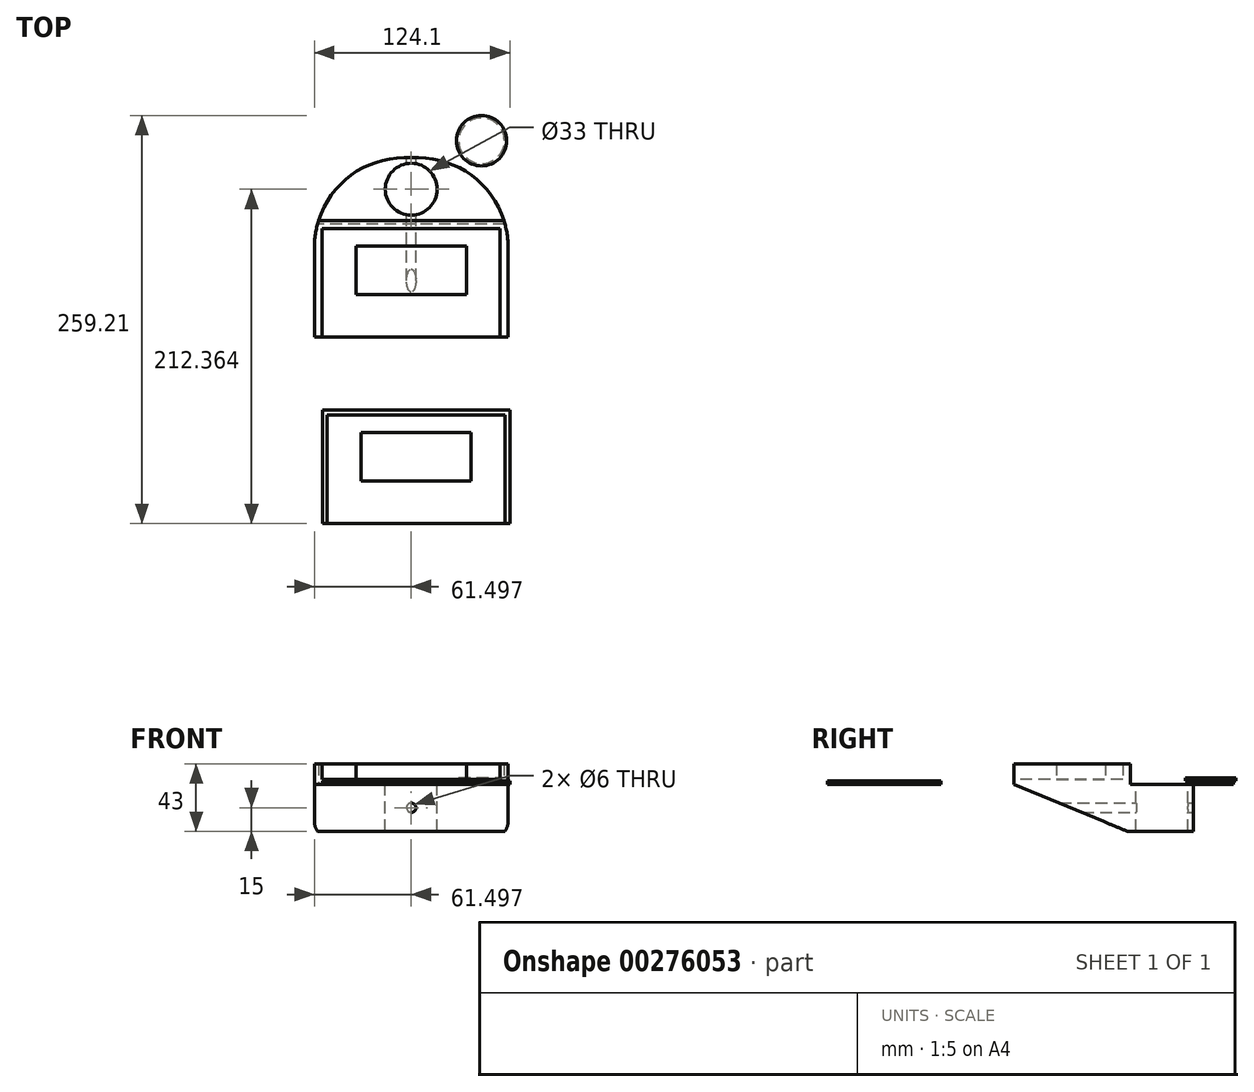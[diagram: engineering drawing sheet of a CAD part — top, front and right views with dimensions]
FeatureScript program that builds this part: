
annotation { "Feature Type Name" : "Feature", "Feature Type Description" : "" }
export const myFeature = defineFeature(function(context is Context, id is Id, definition is map)
    precondition{}
    {
        {
            var Q0;
            Q0=qCreatedBy(makeId("Top.planeOp"),FACE);
            var sketch = newSketch(context, id + "F0", { "sketchPlane" : qUnion([Q0])});
            skCircle(sketch, "E0", {"center": v(-51.44, 51.07) * mm, "radius": 14.5 * mm});
            skSolve(sketch);
        }
        {
            var Q0;
            Q0 = qSketchRegion(id + "F0", true);
            extrude(context, id + "F1", {"entities" : qUnion([Q0]), "depth" : 35 * mm});
        }
        {
            var Q0;
            Q0=makeQuery(id+"F1.opExtrude","CAP_FACE",FACE,{"disambiguationData":[OSD([sQuery(id+"F0.wireOp",EDGE,"E0")])],"isStart":false});
            var sketch = newSketch(context, id + "F2", { "sketchPlane" : qUnion([Q0])});
            skCircle(sketch, "E1", {"center": v(-51.44, 51.07) * mm, "radius": 16 * mm});
            skSolve(sketch);
        }
        {
            var Q0;
            Q0 = qSketchRegion(id + "F2", true);
            extrude(context, id + "F3", {"entities" : qUnion([Q0]), "operationType" : NewBodyOperationType.ADD, "depth" : 3 * mm});
        }
        {
            var Q0;
            Q0=makeQuery(id+"F3.opExtrude","CAP_FACE",FACE,{"disambiguationData":[OSD([sQuery(id+"F2.wireOp",EDGE,"E1")])],"isStart":false});
            var sketch = newSketch(context, id + "F4", { "sketchPlane" : qUnion([Q0])});
            skCircle(sketch, "E2", {"center": v(-51.44, 51.07) * mm, "radius": 14.5 * mm});
            skSolve(sketch);
        }
        {
            var Q0;
            Q0 = qSketchRegion(id + "F4", true);
            extrude(context, id + "F5", {"entities" : qUnion([Q0]), "operationType" : NewBodyOperationType.ADD, "depth" : 35 * mm});
        }
        {
            var Q0;
            Q0=qCreatedBy(makeId("Top.planeOp"),FACE);
            var sketch = newSketch(context, id + "F6", { "sketchPlane" : qUnion([Q0])});
            skLineSegment(sketch, "E3.bottom", {"start": v(-44.58, 8.17) * mm, "end": v(68.42, 8.17) * mm});
            skLineSegment(sketch, "E3.top", {"start": v(-44.58, -60.83) * mm, "end": v(68.42, -60.83) * mm});
            skLineSegment(sketch, "E3.left", {"start": v(-44.58, 8.17) * mm, "end": v(-44.58, -60.83) * mm});
            skLineSegment(sketch, "E3.right", {"start": v(68.42, 8.17) * mm, "end": v(68.42, -60.83) * mm});
            skSolve(sketch);
        }
        {
            var Q0;
            Q0 = qSketchRegion(id + "F6", true);
            extrude(context, id + "F7", {"entities" : qUnion([Q0]), "depth" : 3 * mm});
        }
        {
            var Q0;
            Q0=makeQuery(id+"F7.opExtrude","CAP_FACE",FACE,{"disambiguationData":[OSD([sQuery(id+"F6.wireOp",EDGE,"E3.bottom"),sQuery(id+"F6.wireOp",EDGE,"E3.top"),sQuery(id+"F6.wireOp",EDGE,"E3.left"),sQuery(id+"F6.wireOp",EDGE,"E3.right")])],"isStart":false});
            var sketch = newSketch(context, id + "F8", { "sketchPlane" : qUnion([Q0])});
            skLineSegment(sketch, "E4.bottom", {"start": v(46.92, -33.83) * mm, "end": v(-23.08, -33.83) * mm});
            skLineSegment(sketch, "E4.top", {"start": v(46.92, -2.83) * mm, "end": v(-23.08, -2.83) * mm});
            skLineSegment(sketch, "E4.left", {"start": v(46.92, -33.83) * mm, "end": v(46.92, -2.83) * mm});
            skLineSegment(sketch, "E4.right", {"start": v(-23.08, -33.83) * mm, "end": v(-23.08, -2.83) * mm});
            skPoint(sketch, "E4.middle", {"position": v(11.92, -18.33) * mm});
            skPoint(sketch, "E4.middle.positionSnap0", {"position": v(11.92, 8.17) * mm});
            skPoint(sketch, "E4.centerSnap0", {"position": v(11.92, 8.17) * mm});
            skSolve(sketch);
        }
        {
            var Q0;
            Q0 = qSketchRegion(id + "F8", true);
            extrude(context, id + "F9", {"entities" : qUnion([Q0]), "operationType" : NewBodyOperationType.ADD, "depth" : 10 * mm});
        }
        {
            var Q0;
            Q0=makeQuery(id+"F7.opExtrude","SWEPT_FACE",FACE,{"disambiguationData":[OSD([sQuery(id+"F6.wireOp",EDGE,"E3.right")])]});
            var sketch = newSketch(context, id + "F10", { "sketchPlane" : qUnion([Q0])});
            skLineSegment(sketch, "E5.bottom", {"start": v(-60.83, 0) * mm, "end": v(8.17, 0) * mm});
            skLineSegment(sketch, "E5.top", {"start": v(-60.83, 13) * mm, "end": v(8.17, 13) * mm});
            skLineSegment(sketch, "E5.left", {"start": v(-60.83, 0) * mm, "end": v(-60.83, 13) * mm});
            skLineSegment(sketch, "E5.right", {"start": v(8.17, 0) * mm, "end": v(8.17, 13) * mm});
            skSolve(sketch);
        }
        {
            var Q0;
            Q0 = qSketchRegion(id + "F10", true);
            extrude(context, id + "F11", {"entities" : qUnion([Q0]), "operationType" : NewBodyOperationType.ADD, "depth" : 5 * mm});
        }
        {
            var Q0;
            Q0=makeQuery(id+"F11.boolean.opBoolean","MERGE",FACE,{"derivedFrom":[makeQuery(id+"F7.opExtrude","SWEPT_FACE",FACE,{"disambiguationData":[OSD([sQuery(id+"F6.wireOp",EDGE,"E3.bottom")])]}),makeQuery(id+"F11.opExtrude","SWEPT_FACE",FACE,{"disambiguationData":[OSD([sQuery(id+"F10.wireOp",EDGE,"E5.right")])]})]});
            var sketch = newSketch(context, id + "F12", { "sketchPlane" : qUnion([Q0])});
            skLineSegment(sketch, "E6.bottom", {"start": v(-73.42, 13) * mm, "end": v(44.58, 13) * mm});
            skLineSegment(sketch, "E6.top", {"start": v(-73.42, 0) * mm, "end": v(44.58, 0) * mm});
            skLineSegment(sketch, "E6.left", {"start": v(-73.42, 13) * mm, "end": v(-73.42, 0) * mm});
            skLineSegment(sketch, "E6.right", {"start": v(44.58, 13) * mm, "end": v(44.58, 0) * mm});
            skSolve(sketch);
        }
        {
            var Q0;
            Q0 = qSketchRegion(id + "F12", true);
            extrude(context, id + "F13", {"entities" : qUnion([Q0]), "operationType" : NewBodyOperationType.ADD, "depth" : 5 * mm});
        }
        {
            var Q0;
            Q0=makeQuery(id+"F13.boolean.opBoolean","MERGE",FACE,{"derivedFrom":[makeQuery(id+"F7.opExtrude","SWEPT_FACE",FACE,{"disambiguationData":[OSD([sQuery(id+"F6.wireOp",EDGE,"E3.left")])]}),makeQuery(id+"F13.opExtrude","SWEPT_FACE",FACE,{"disambiguationData":[OSD([sQuery(id+"F12.wireOp",EDGE,"E6.right")])]})]});
            var sketch = newSketch(context, id + "F14", { "sketchPlane" : qUnion([Q0])});
            skLineSegment(sketch, "E7.bottom", {"start": v(-13.17, 13) * mm, "end": v(60.83, 13) * mm});
            skLineSegment(sketch, "E7.top", {"start": v(-13.17, 0) * mm, "end": v(60.83, 0) * mm});
            skLineSegment(sketch, "E7.left", {"start": v(-13.17, 13) * mm, "end": v(-13.17, 0) * mm});
            skLineSegment(sketch, "E7.right", {"start": v(60.83, 13) * mm, "end": v(60.83, 0) * mm});
            skSolve(sketch);
        }
        {
            var Q0;
            Q0 = qSketchRegion(id + "F14", true);
            extrude(context, id + "F15", {"entities" : qUnion([Q0]), "operationType" : NewBodyOperationType.ADD, "depth" : 5 * mm});
        }
        {
            var Q0;
            Q0=makeQuery(id+"F15.boolean.opBoolean","MERGE",FACE,{"derivedFrom":[makeQuery(id+"F13.boolean.opBoolean","MERGE",FACE,{"derivedFrom":[makeQuery(id+"F11.boolean.opBoolean","MERGE",FACE,{"derivedFrom":[makeQuery(id+"F7.opExtrude","CAP_FACE",FACE,{"disambiguationData":[OSD([sQuery(id+"F6.wireOp",EDGE,"E3.bottom"),sQuery(id+"F6.wireOp",EDGE,"E3.top"),sQuery(id+"F6.wireOp",EDGE,"E3.left"),sQuery(id+"F6.wireOp",EDGE,"E3.right")])],"isStart":true}),makeQuery(id+"F11.opExtrude","SWEPT_FACE",FACE,{"disambiguationData":[OSD([sQuery(id+"F10.wireOp",EDGE,"E5.bottom")])]})]}),makeQuery(id+"F13.opExtrude","SWEPT_FACE",FACE,{"disambiguationData":[OSD([sQuery(id+"F12.wireOp",EDGE,"E6.top")])]})]}),makeQuery(id+"F15.opExtrude","SWEPT_FACE",FACE,{"disambiguationData":[OSD([sQuery(id+"F14.wireOp",EDGE,"E7.top")])]})]});
            var sketch = newSketch(context, id + "F16", { "sketchPlane" : qUnion([Q0])});
            skLineSegment(sketch, "E8.bottom", {"start": v(73.42, -13.17) * mm, "end": v(-49.58, -13.17) * mm});
            skLineSegment(sketch, "E8.top", {"start": v(73.42, 60.83) * mm, "end": v(-49.58, 60.83) * mm});
            skLineSegment(sketch, "E8.left", {"start": v(73.42, -13.17) * mm, "end": v(73.42, 60.83) * mm});
            skLineSegment(sketch, "E8.right", {"start": v(-49.58, -13.17) * mm, "end": v(-49.58, 60.83) * mm});
            skSolve(sketch);
        }
        {
            var Q0;
            Q0 = qSketchRegion(id + "F16", true);
            extrude(context, id + "F17", {"entities" : qUnion([Q0]), "operationType" : NewBodyOperationType.ADD, "depth" : 30 * mm});
        }
        {
            var Q0;
            Q0=makeQuery(id+"F17.boolean.opBoolean","MERGE",FACE,{"derivedFrom":[makeQuery(id+"F15.boolean.opBoolean","MERGE",FACE,{"derivedFrom":[makeQuery(id+"F13.opExtrude","CAP_FACE",FACE,{"disambiguationData":[OSD([sQuery(id+"F12.wireOp",EDGE,"E6.bottom"),sQuery(id+"F12.wireOp",EDGE,"E6.top"),sQuery(id+"F12.wireOp",EDGE,"E6.left"),sQuery(id+"F12.wireOp",EDGE,"E6.right")])],"isStart":false}),makeQuery(id+"F15.opExtrude","SWEPT_FACE",FACE,{"disambiguationData":[OSD([sQuery(id+"F14.wireOp",EDGE,"E7.left")])]})]}),makeQuery(id+"F17.opExtrude","SWEPT_FACE",FACE,{"disambiguationData":[OSD([sQuery(id+"F16.wireOp",EDGE,"E8.bottom")])]})]});
            var sketch = newSketch(context, id + "F18", { "sketchPlane" : qUnion([Q0])});
            skPoint(sketch, "E9", {"position": v(-11.92, 0) * mm});
            skPoint(sketch, "E9.positionSnap0", {"position": v(-11.92, -30) * mm});
            skLineSegment(sketch, "E10.bottom", {"start": v(-73.42, 0) * mm, "end": v(49.58, 0) * mm});
            skLineSegment(sketch, "E10.top", {"start": v(-73.42, -30) * mm, "end": v(49.58, -30) * mm});
            skLineSegment(sketch, "E10.left", {"start": v(-73.42, 0) * mm, "end": v(-73.42, -30) * mm});
            skLineSegment(sketch, "E10.right", {"start": v(49.58, 0) * mm, "end": v(49.58, -30) * mm});
            skSolve(sketch);
        }
        {
            var Q0;
            Q0 = qSketchRegion(id + "F18", true);
            extrude(context, id + "F19", {"entities" : qUnion([Q0]), "operationType" : NewBodyOperationType.ADD, "depth" : 40 * mm});
        }
        {
            var Q0;
            Q0=makeQuery(id+"F19.opExtrude","SWEPT_FACE",FACE,{"disambiguationData":[OSD([sQuery(id+"F18.wireOp",EDGE,"E10.bottom")])]});
            var sketch = newSketch(context, id + "F20", { "sketchPlane" : qUnion([Q0])});
            skCircle(sketch, "E11", {"center": v(11.92, 33.17) * mm, "radius": 16.5 * mm});
            skPoint(sketch, "E11.centerSnap0", {"position": v(73.42, 33.17) * mm});
            skPoint(sketch, "E11.centerSnap1", {"position": v(11.92, 53.17) * mm});
            skSolve(sketch);
        }
        {
            var Q0;
            Q0 = qSketchRegion(id + "F20", true);
            extrude(context, id + "F21", {"entities" : qUnion([Q0]), "operationType" : NewBodyOperationType.REMOVE, "endBound" : BoundingType.THROUGH_ALL, "oppositeDirection" : true, "depth" : 25 * mm});
        }
        {
            var Q0;
            Q0=makeQuery(id+"F17.opExtrude","CAP_EDGE",EDGE,{"disambiguationData":[OSD([sQuery(id+"F16.wireOp",EDGE,"E8.top")])],"isStart":false});
            chamfer(context, id + "F22", {"entities" : qUnion([Q0]), "chamferType" : ChamferType.TWO_OFFSETS, "width1" : 30 * mm, "oppositeDirection" : false, "width2" : 72 * mm, "tangentPropagation" : true});
        }
        {
            var Q0;
            Q0=makeQuery(id+"F19.opExtrude","CAP_EDGE",EDGE,{"disambiguationData":[OSD([sQuery(id+"F18.wireOp",EDGE,"E10.left")])],"isStart":false});
            fillet(context, id + "F23", {"entities" : qUnion([Q0]), "radius" : 57 * mm, "tangentPropagation" : true, "allowEdgeOverflow" : false});
        }
        {
            var Q0;
            Q0=makeQuery(id+"F19.opExtrude","CAP_EDGE",EDGE,{"disambiguationData":[OSD([sQuery(id+"F18.wireOp",EDGE,"E10.right")])],"isStart":false});
            fillet(context, id + "F24", {"entities" : qUnion([Q0]), "radius" : 57 * mm, "tangentPropagation" : true, "allowEdgeOverflow" : false});
        }
        {
            var Q0;
            Q0=makeQuery(id+"F19.opExtrude","CAP_FACE",FACE,{"disambiguationData":[OSD([sQuery(id+"F18.wireOp",EDGE,"E10.bottom"),sQuery(id+"F18.wireOp",EDGE,"E10.top"),sQuery(id+"F18.wireOp",EDGE,"E10.left"),sQuery(id+"F18.wireOp",EDGE,"E10.right")])],"isStart":false});
            var sketch = newSketch(context, id + "F25", { "sketchPlane" : qUnion([Q0])});
            skCircle(sketch, "E12", {"center": v(-11.92, -15) * mm, "radius": 3 * mm});
            skPoint(sketch, "E12.centerSnap0", {"position": v(-7.42, -15) * mm});
            skPoint(sketch, "E12.centerSnap1", {"position": v(-11.92, 0) * mm});
            skSolve(sketch);
        }
        {
            var Q0;
            Q0 = qSketchRegion(id + "F25", true);
            extrude(context, id + "F26", {"entities" : qUnion([Q0]), "operationType" : NewBodyOperationType.REMOVE, "endBound" : BoundingType.THROUGH_ALL, "oppositeDirection" : true, "depth" : 25 * mm});
        }
        {
            var Q0;
            Q0=qCreatedBy(makeId("Top.planeOp"),FACE);
            var sketch = newSketch(context, id + "F27", { "sketchPlane" : qUnion([Q0])});
            skCircle(sketch, "E13", {"center": v(56.55, 64.02) * mm, "radius": 14.5 * mm});
            skSolve(sketch);
        }
        {
            var Q0;
            Q0 = qSketchRegion(id + "F27", true);
            extrude(context, id + "F28", {"entities" : qUnion([Q0]), "depth" : 2 * mm});
        }
        {
            var Q0;
            Q0=makeQuery(id+"F28.opExtrude","CAP_FACE",FACE,{"disambiguationData":[OSD([sQuery(id+"F27.wireOp",EDGE,"E13")])],"isStart":false});
            var sketch = newSketch(context, id + "F29", { "sketchPlane" : qUnion([Q0])});
            skCircle(sketch, "E14", {"center": v(56.55, 64.02) * mm, "radius": 16 * mm});
            skSolve(sketch);
        }
        {
            var Q0;
            Q0 = qSketchRegion(id + "F29", true);
            extrude(context, id + "F30", {"entities" : qUnion([Q0]), "operationType" : NewBodyOperationType.ADD, "depth" : 2 * mm});
        }
        {
            var Q0;
            Q0=qCreatedBy(makeId("Top.planeOp"),FACE);
            var sketch = newSketch(context, id + "F31", { "sketchPlane" : qUnion([Q0])});
            skLineSegment(sketch, "E15.bottom", {"start": v(-44.48, -107.19) * mm, "end": v(74.52, -107.19) * mm});
            skLineSegment(sketch, "E15.top", {"start": v(-44.48, -179.19) * mm, "end": v(74.52, -179.19) * mm});
            skLineSegment(sketch, "E15.left", {"start": v(-44.48, -107.19) * mm, "end": v(-44.48, -179.19) * mm});
            skLineSegment(sketch, "E15.right", {"start": v(74.52, -107.19) * mm, "end": v(74.52, -179.19) * mm});
            skSolve(sketch);
        }
        {
            var Q0;
            Q0 = qSketchRegion(id + "F31", true);
            extrude(context, id + "F32", {"entities" : qUnion([Q0]), "depth" : 1 * mm});
        }
        {
            var Q0;
            Q0=makeQuery(id+"F32.opExtrude","CAP_FACE",FACE,{"disambiguationData":[OSD([sQuery(id+"F31.wireOp",EDGE,"E15.bottom"),sQuery(id+"F31.wireOp",EDGE,"E15.top"),sQuery(id+"F31.wireOp",EDGE,"E15.left"),sQuery(id+"F31.wireOp",EDGE,"E15.right")])],"isStart":false});
            var sketch = newSketch(context, id + "F33", { "sketchPlane" : qUnion([Q0])});
            skLineSegment(sketch, "E16.bottom", {"start": v(-44.48, -107.19) * mm, "end": v(-41.48, -107.19) * mm});
            skLineSegment(sketch, "E16.top", {"start": v(-44.48, -179.19) * mm, "end": v(-41.48, -179.19) * mm});
            skLineSegment(sketch, "E16.left", {"start": v(-44.48, -107.19) * mm, "end": v(-44.48, -179.19) * mm});
            skLineSegment(sketch, "E16.right", {"start": v(-41.48, -107.19) * mm, "end": v(-41.48, -179.19) * mm});
            skLineSegment(sketch, "E17.bottom", {"start": v(-44.48, -107.19) * mm, "end": v(74.52, -107.19) * mm});
            skLineSegment(sketch, "E17.top", {"start": v(-44.48, -110.19) * mm, "end": v(74.52, -110.19) * mm});
            skLineSegment(sketch, "E17.left", {"start": v(-44.48, -107.19) * mm, "end": v(-44.48, -110.19) * mm});
            skLineSegment(sketch, "E17.right", {"start": v(74.52, -107.19) * mm, "end": v(74.52, -110.19) * mm});
            skLineSegment(sketch, "E18.bottom", {"start": v(74.52, -107.19) * mm, "end": v(71.52, -107.19) * mm});
            skLineSegment(sketch, "E18.top", {"start": v(74.52, -179.19) * mm, "end": v(71.52, -179.19) * mm});
            skLineSegment(sketch, "E18.left", {"start": v(74.52, -107.19) * mm, "end": v(74.52, -179.19) * mm});
            skLineSegment(sketch, "E18.right", {"start": v(71.52, -107.19) * mm, "end": v(71.52, -179.19) * mm});
            skSolve(sketch);
        }
        {
            var Q0;
            Q0 = qSketchRegion(id + "F33", true);
            extrude(context, id + "F34", {"entities" : qUnion([Q0]), "operationType" : NewBodyOperationType.ADD, "depth" : 1 * mm});
        }
        {
            var Q0;
            Q0=makeQuery(id+"F32.opExtrude","CAP_FACE",FACE,{"disambiguationData":[OSD([sQuery(id+"F31.wireOp",EDGE,"E15.bottom"),sQuery(id+"F31.wireOp",EDGE,"E15.top"),sQuery(id+"F31.wireOp",EDGE,"E15.left"),sQuery(id+"F31.wireOp",EDGE,"E15.right")])],"isStart":false});
            var sketch = newSketch(context, id + "F35", { "sketchPlane" : qUnion([Q0])});
            skLineSegment(sketch, "E19.bottom", {"start": v(50.02, -152.19) * mm, "end": v(-19.98, -152.19) * mm});
            skLineSegment(sketch, "E19.top", {"start": v(50.02, -121.19) * mm, "end": v(-19.98, -121.19) * mm});
            skLineSegment(sketch, "E19.left", {"start": v(50.02, -152.19) * mm, "end": v(50.02, -121.19) * mm});
            skLineSegment(sketch, "E19.right", {"start": v(-19.98, -152.19) * mm, "end": v(-19.98, -121.19) * mm});
            skPoint(sketch, "E19.middle", {"position": v(15.02, -136.69) * mm});
            skPoint(sketch, "E19.middle.positionSnap0", {"position": v(71.52, -136.69) * mm});
            skPoint(sketch, "E19.middle.positionSnap1", {"position": v(15.02, -110.19) * mm});
            skPoint(sketch, "E19.centerSnap0", {"position": v(71.52, -136.69) * mm});
            skPoint(sketch, "E19.centerSnap1", {"position": v(15.02, -110.19) * mm});
            skSolve(sketch);
        }
        {
            var Q0;
            Q0 = qSketchRegion(id + "F35", true);
            extrude(context, id + "F36", {"entities" : qUnion([Q0]), "operationType" : NewBodyOperationType.ADD, "depth" : 1 * mm});
        }
    });
